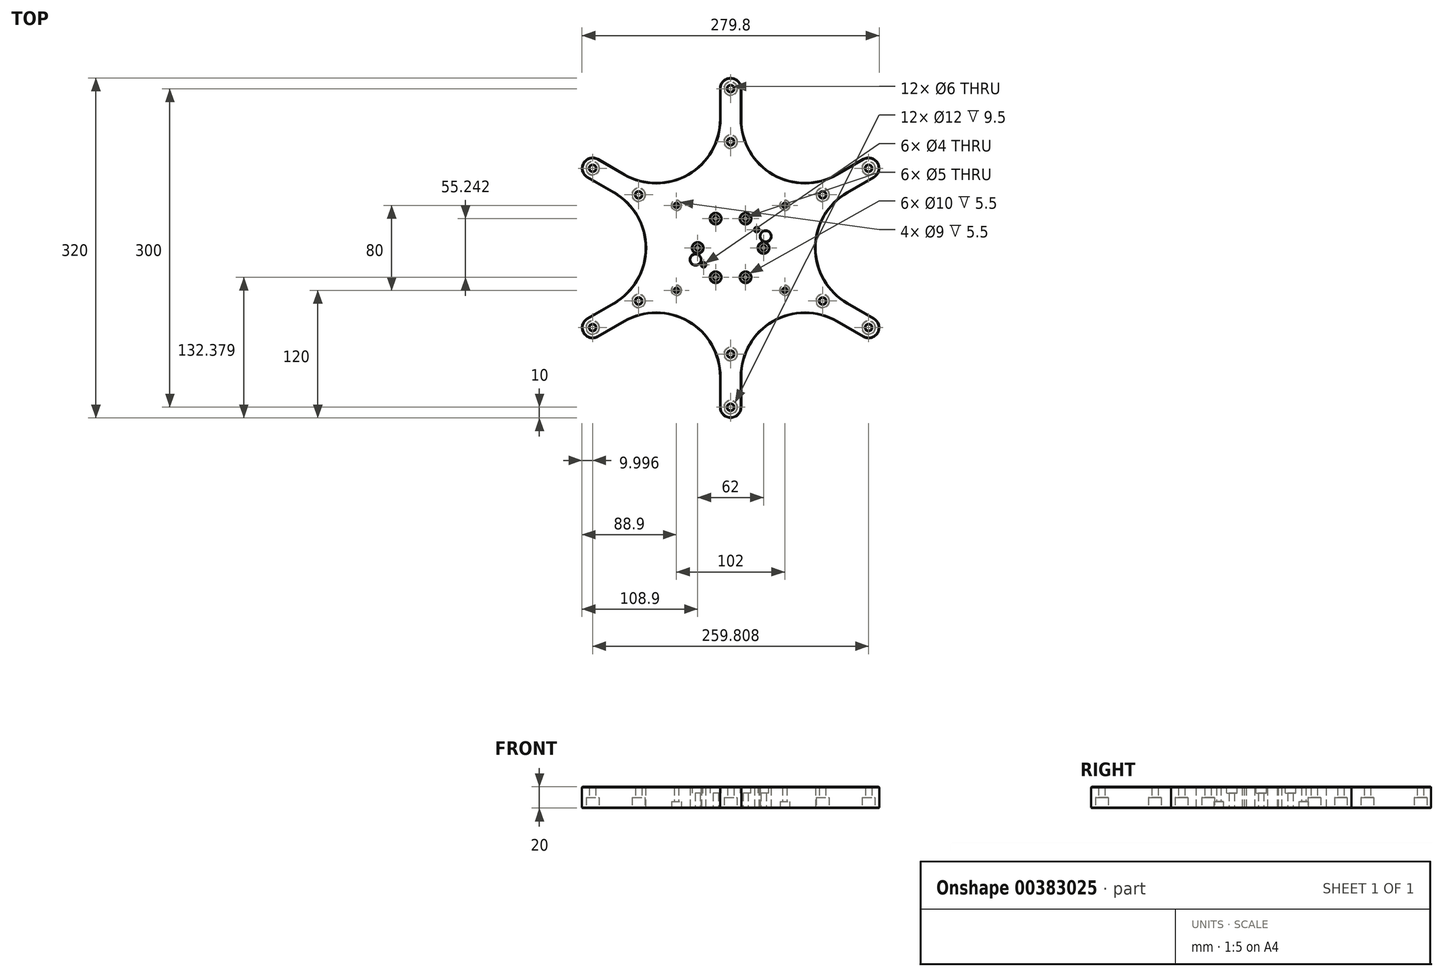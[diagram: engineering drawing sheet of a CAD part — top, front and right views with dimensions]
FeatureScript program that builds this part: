
annotation { "Feature Type Name" : "Feature", "Feature Type Description" : "" }
export const myFeature = defineFeature(function(context is Context, id is Id, definition is map)
    precondition{}
    {
        {
            var Q0;
            Q0=qCreatedBy(makeId("Top.planeOp"),FACE);
            var sketch = newSketch(context, id + "F0", { "sketchPlane" : qUnion([Q0])});
            skCircle(sketch, "E0", {"center": v(31, 0) * mm, "radius": 2.5 * mm});
            skCircle(sketch, "E1.1.0", {"center": v(14.07, 27.62) * mm, "radius": 2.5 * mm});
            skCircle(sketch, "E1.2.0", {"center": v(-14.07, 27.62) * mm, "radius": 2.5 * mm});
            skCircle(sketch, "E1.3.0", {"center": v(-31, 0) * mm, "radius": 2.5 * mm});
            skCircle(sketch, "E1.4.0", {"center": v(-14.07, -27.62) * mm, "radius": 2.5 * mm});
            skCircle(sketch, "E1.5.0", {"center": v(14.07, -27.62) * mm, "radius": 2.5 * mm});
            skPoint(sketch, "E1.center", {"position": v(0, 0) * mm});
            skLineSegment(sketch, "E2.bottom", {"start": v(-56, 45) * mm, "end": v(56, 45) * mm});
            skLineSegment(sketch, "E2.top", {"start": v(-56, -45) * mm, "end": v(56, -45) * mm});
            skLineSegment(sketch, "E2.left", {"start": v(-56, 45) * mm, "end": v(-56, -45) * mm});
            skLineSegment(sketch, "E2.right", {"start": v(56, 45) * mm, "end": v(56, -45) * mm});
            skLineSegment(sketch, "E3", {"start": v(-37.37, 11) * mm, "end": v(33, 11) * mm, "construction": true});
            skLineSegment(sketch, "E4", {"start": v(33, 11) * mm, "end": v(33, -11) * mm, "construction": true});
            skLineSegment(sketch, "E5", {"start": v(33, -11) * mm, "end": v(-33, -11) * mm, "construction": true});
            skLineSegment(sketch, "E6", {"start": v(-33, -11) * mm, "end": v(-33, 11) * mm, "construction": true});
            skCircle(sketch, "E7", {"center": v(-33, 11) * mm, "radius": 5 * mm, "construction": true});
            skCircle(sketch, "E8", {"center": v(33, 11) * mm, "radius": 5 * mm});
            skCircle(sketch, "E9", {"center": v(33, -11) * mm, "radius": 5 * mm, "construction": true});
            skCircle(sketch, "E10", {"center": v(-33, -11) * mm, "radius": 5 * mm});
            skLineSegment(sketch, "E11.bottom", {"start": v(-51, 40) * mm, "end": v(51, 40) * mm, "construction": true});
            skLineSegment(sketch, "E11.top", {"start": v(-51, -40) * mm, "end": v(51, -40) * mm, "construction": true});
            skLineSegment(sketch, "E11.left", {"start": v(-51, 40) * mm, "end": v(-51, -40) * mm, "construction": true});
            skLineSegment(sketch, "E11.right", {"start": v(51, 40) * mm, "end": v(51, -40) * mm, "construction": true});
            skCircle(sketch, "E12", {"center": v(-51, 40) * mm, "radius": 2 * mm});
            skCircle(sketch, "E13", {"center": v(51, 40) * mm, "radius": 2 * mm});
            skCircle(sketch, "E14", {"center": v(51, -40) * mm, "radius": 2 * mm});
            skCircle(sketch, "E15", {"center": v(-51, -40) * mm, "radius": 2 * mm});
            skLineSegment(sketch, "E16", {"start": v(-14.07, -27.62) * mm, "end": v(14.07, 27.62) * mm, "construction": true});
            skLineSegment(sketch, "E17", {"start": v(14.07, -27.62) * mm, "end": v(-14.07, 27.62) * mm, "construction": true});
            skLineSegment(sketch, "E18", {"start": v(55.41, 17.21) * mm, "end": v(-51.67, 17.2) * mm, "construction": true});
            skLineSegment(sketch, "E19", {"start": v(24.57, -95.5) * mm, "end": v(24.57, 92.97) * mm, "construction": true});
            skCircle(sketch, "E20", {"center": v(24.57, 17.21) * mm, "radius": 2 * mm});
            skCircle(sketch, "E21", {"center": v(-25.44, -15.9) * mm, "radius": 2 * mm});
            skSolve(sketch);
        }
        {
            var Q0;
            Q0 = qSketchRegion(id + "F0", true);
            extrude(context, id + "F1", {"entities" : qUnion([Q0]), "depth" : 20 * mm, "offsetDistance" : 25 * mm});
        }
        {
            var Q0;
            Q0=makeQuery(id+"F1.opExtrude","SWEPT_EDGE",EDGE,{"disambiguationData":[OSD([sQuery(id+"F0.wireOp",EDGE,"E2.top"),sQuery(id+"F0.wireOp",EDGE,"E2.left")])]});
            var Q1;
            Q1=makeQuery(id+"F1.opExtrude","SWEPT_EDGE",EDGE,{"disambiguationData":[OSD([sQuery(id+"F0.wireOp",EDGE,"E2.bottom"),sQuery(id+"F0.wireOp",EDGE,"E2.left")])]});
            var Q2;
            Q2=makeQuery(id+"F1.opExtrude","SWEPT_EDGE",EDGE,{"disambiguationData":[OSD([sQuery(id+"F0.wireOp",EDGE,"E2.top"),sQuery(id+"F0.wireOp",EDGE,"E2.right")])]});
            var Q3;
            Q3=makeQuery(id+"F1.opExtrude","SWEPT_EDGE",EDGE,{"disambiguationData":[OSD([sQuery(id+"F0.wireOp",EDGE,"E2.bottom"),sQuery(id+"F0.wireOp",EDGE,"E2.right")])]});
            chamfer(context, id + "F2", {"entities" : qUnion([Q0, Q1, Q2, Q3]), "width" : 2.5 * mm, "tangentPropagation" : true});
        }
        {
            var Q0;
            Q0=makeQuery(id+"F1.opExtrude","CAP_FACE",FACE,{"disambiguationData":[OSD([sQuery(id+"F0.wireOp",EDGE,"E0"),sQuery(id+"F0.wireOp",EDGE,"E1.1.0"),sQuery(id+"F0.wireOp",EDGE,"E1.2.0"),sQuery(id+"F0.wireOp",EDGE,"E1.3.0"),sQuery(id+"F0.wireOp",EDGE,"E1.4.0"),sQuery(id+"F0.wireOp",EDGE,"E1.5.0"),sQuery(id+"F0.wireOp",EDGE,"E2.bottom"),sQuery(id+"F0.wireOp",EDGE,"E2.top"),sQuery(id+"F0.wireOp",EDGE,"E2.left"),sQuery(id+"F0.wireOp",EDGE,"E2.right"),sQuery(id+"F0.wireOp",EDGE,"E7"),sQuery(id+"F0.wireOp",EDGE,"E8"),sQuery(id+"F0.wireOp",EDGE,"E9"),sQuery(id+"F0.wireOp",EDGE,"E10"),sQuery(id+"F0.wireOp",EDGE,"E12"),sQuery(id+"F0.wireOp",EDGE,"E13"),sQuery(id+"F0.wireOp",EDGE,"E14"),sQuery(id+"F0.wireOp",EDGE,"E15")])],"isStart":false});
            var sketch = newSketch(context, id + "F3", { "sketchPlane" : qUnion([Q0])});
            skCircle(sketch, "E22", {"center": v(-14.07, 27.62) * mm, "radius": 5 * mm});
            skCircle(sketch, "E23", {"center": v(14.07, 27.62) * mm, "radius": 5 * mm});
            skCircle(sketch, "E24", {"center": v(31, 0) * mm, "radius": 5 * mm});
            skCircle(sketch, "E25", {"center": v(14.07, -27.62) * mm, "radius": 5 * mm});
            skCircle(sketch, "E26", {"center": v(-14.07, -27.62) * mm, "radius": 5 * mm});
            skCircle(sketch, "E27", {"center": v(-31, 0) * mm, "radius": 5 * mm});
            skSolve(sketch);
        }
        {
            var Q0;
            Q0 = qSketchRegion(id + "F3", true);
            extrude(context, id + "F4", {"entities" : qUnion([Q0]), "operationType" : NewBodyOperationType.REMOVE, "oppositeDirection" : true, "depth" : 6 * mm, "offsetDistance" : 25 * mm});
        }
        {
            var Q0;
            Q0=makeQuery(id+"F1.opExtrude","CAP_FACE",FACE,{"disambiguationData":[OSD([sQuery(id+"F0.wireOp",EDGE,"E0"),sQuery(id+"F0.wireOp",EDGE,"E1.1.0"),sQuery(id+"F0.wireOp",EDGE,"E1.2.0"),sQuery(id+"F0.wireOp",EDGE,"E1.3.0"),sQuery(id+"F0.wireOp",EDGE,"E1.4.0"),sQuery(id+"F0.wireOp",EDGE,"E1.5.0"),sQuery(id+"F0.wireOp",EDGE,"E2.bottom"),sQuery(id+"F0.wireOp",EDGE,"E2.top"),sQuery(id+"F0.wireOp",EDGE,"E2.left"),sQuery(id+"F0.wireOp",EDGE,"E2.right"),sQuery(id+"F0.wireOp",EDGE,"E8"),sQuery(id+"F0.wireOp",EDGE,"E10"),sQuery(id+"F0.wireOp",EDGE,"E12"),sQuery(id+"F0.wireOp",EDGE,"E13"),sQuery(id+"F0.wireOp",EDGE,"E14"),sQuery(id+"F0.wireOp",EDGE,"E15")])],"isStart":true});
            var sketch = newSketch(context, id + "F5", { "sketchPlane" : qUnion([Q0])});
            skCircle(sketch, "E28", {"center": v(-51, 40) * mm, "radius": 4.5 * mm});
            skCircle(sketch, "E29", {"center": v(51, 40) * mm, "radius": 4.5 * mm});
            skCircle(sketch, "E30", {"center": v(51, -40) * mm, "radius": 4.5 * mm});
            skCircle(sketch, "E31", {"center": v(-51, -40) * mm, "radius": 4.5 * mm});
            skSolve(sketch);
        }
        {
            var Q0;
            Q0 = qSketchRegion(id + "F5", true);
            extrude(context, id + "F6", {"entities" : qUnion([Q0]), "operationType" : NewBodyOperationType.REMOVE, "oppositeDirection" : true, "depth" : 6 * mm, "offsetDistance" : 25 * mm});
        }
        {
            var Q0;
            Q0=makeQuery(id+"F1.opExtrude","CAP_FACE",FACE,{"disambiguationData":[OSD([sQuery(id+"F0.wireOp",EDGE,"E0"),sQuery(id+"F0.wireOp",EDGE,"E1.1.0"),sQuery(id+"F0.wireOp",EDGE,"E1.2.0"),sQuery(id+"F0.wireOp",EDGE,"E1.3.0"),sQuery(id+"F0.wireOp",EDGE,"E1.4.0"),sQuery(id+"F0.wireOp",EDGE,"E1.5.0"),sQuery(id+"F0.wireOp",EDGE,"E2.bottom"),sQuery(id+"F0.wireOp",EDGE,"E2.top"),sQuery(id+"F0.wireOp",EDGE,"E2.left"),sQuery(id+"F0.wireOp",EDGE,"E2.right"),sQuery(id+"F0.wireOp",EDGE,"E8"),sQuery(id+"F0.wireOp",EDGE,"E10"),sQuery(id+"F0.wireOp",EDGE,"E12"),sQuery(id+"F0.wireOp",EDGE,"E13"),sQuery(id+"F0.wireOp",EDGE,"E14"),sQuery(id+"F0.wireOp",EDGE,"E15")])],"isStart":true});
            var sketch = newSketch(context, id + "F7", { "sketchPlane" : qUnion([Q0])});
            skLineSegment(sketch, "E32", {"start": v(0, 0) * mm, "end": v(0, 187.02) * mm, "construction": true});
            skCircle(sketch, "E33", {"center": v(0, 150) * mm, "radius": 3 * mm});
            skCircle(sketch, "E34", {"center": v(0, 100) * mm, "radius": 3 * mm});
            skCircle(sketch, "E35", {"center": v(0, 150) * mm, "radius": 10 * mm, "construction": true});
            skLineSegment(sketch, "E36", {"start": v(-10, 150) * mm, "end": v(-10, 35.87) * mm, "construction": true});
            skLineSegment(sketch, "E37", {"start": v(10, 39.07) * mm, "end": v(10, 150) * mm, "construction": true});
            skLineSegment(sketch, "E38.1.0", {"start": v(0, 0) * mm, "end": v(-161.97, 93.51) * mm, "construction": true});
            skCircle(sketch, "E38.1.1", {"center": v(-129.9, 75) * mm, "radius": 10 * mm, "construction": true});
            skCircle(sketch, "E38.1.2", {"center": v(-129.9, 75) * mm, "radius": 3 * mm});
            skLineSegment(sketch, "E38.1.3", {"start": v(-134.9, 66.34) * mm, "end": v(-36.06, 9.27) * mm, "construction": true});
            skLineSegment(sketch, "E38.1.4", {"start": v(-28.84, 28.2) * mm, "end": v(-124.9, 83.66) * mm, "construction": true});
            skCircle(sketch, "E38.1.5", {"center": v(-86.6, 50) * mm, "radius": 3 * mm});
            skLineSegment(sketch, "E38.2.0", {"start": v(0, 0) * mm, "end": v(-161.97, -93.51) * mm, "construction": true});
            skCircle(sketch, "E38.2.1", {"center": v(-129.9, -75) * mm, "radius": 10 * mm, "construction": true});
            skCircle(sketch, "E38.2.2", {"center": v(-129.9, -75) * mm, "radius": 3 * mm});
            skLineSegment(sketch, "E38.2.3", {"start": v(-124.9, -83.66) * mm, "end": v(-26.06, -26.6) * mm, "construction": true});
            skLineSegment(sketch, "E38.2.4", {"start": v(-38.84, -10.88) * mm, "end": v(-134.9, -66.34) * mm, "construction": true});
            skCircle(sketch, "E38.2.5", {"center": v(-86.6, -50) * mm, "radius": 3 * mm});
            skLineSegment(sketch, "E38.3.0", {"start": v(0, 0) * mm, "end": v(0, -187.02) * mm, "construction": true});
            skCircle(sketch, "E38.3.1", {"center": v(0, -150) * mm, "radius": 10 * mm, "construction": true});
            skCircle(sketch, "E38.3.2", {"center": v(0, -150) * mm, "radius": 3 * mm});
            skLineSegment(sketch, "E38.3.3", {"start": v(10, -150) * mm, "end": v(10, -35.87) * mm, "construction": true});
            skLineSegment(sketch, "E38.3.4", {"start": v(-10, -39.07) * mm, "end": v(-10, -150) * mm, "construction": true});
            skCircle(sketch, "E38.3.5", {"center": v(0, -100) * mm, "radius": 3 * mm});
            skLineSegment(sketch, "E38.4.0", {"start": v(0, 0) * mm, "end": v(161.97, -93.51) * mm, "construction": true});
            skCircle(sketch, "E38.4.1", {"center": v(129.9, -75) * mm, "radius": 10 * mm, "construction": true});
            skCircle(sketch, "E38.4.2", {"center": v(129.9, -75) * mm, "radius": 3 * mm});
            skLineSegment(sketch, "E38.4.3", {"start": v(134.9, -66.34) * mm, "end": v(36.06, -9.27) * mm, "construction": true});
            skLineSegment(sketch, "E38.4.4", {"start": v(28.84, -28.2) * mm, "end": v(124.9, -83.66) * mm, "construction": true});
            skCircle(sketch, "E38.4.5", {"center": v(86.6, -50) * mm, "radius": 3 * mm});
            skLineSegment(sketch, "E38.5.0", {"start": v(0, 0) * mm, "end": v(161.97, 93.51) * mm, "construction": true});
            skCircle(sketch, "E38.5.1", {"center": v(129.9, 75) * mm, "radius": 10 * mm, "construction": true});
            skCircle(sketch, "E38.5.2", {"center": v(129.9, 75) * mm, "radius": 3 * mm});
            skLineSegment(sketch, "E38.5.3", {"start": v(124.9, 83.66) * mm, "end": v(26.06, 26.6) * mm, "construction": true});
            skLineSegment(sketch, "E38.5.4", {"start": v(38.84, 10.88) * mm, "end": v(134.9, 66.34) * mm, "construction": true});
            skCircle(sketch, "E38.5.5", {"center": v(86.6, 50) * mm, "radius": 3 * mm});
            skPoint(sketch, "E38.center", {"position": v(0, 0) * mm});
            skArc(sketch, "E39", {"start": v(-100, 69.28) * mm, "mid": v(-40, 69.28) * mm, "end": v(-10, 121.24) * mm});
            skArc(sketch, "E40", {"start": v(10, 121.24) * mm, "mid": v(40, 69.28) * mm, "end": v(100, 69.28) * mm});
            skArc(sketch, "E41", {"start": v(110, 51.96) * mm, "mid": v(80, 0) * mm, "end": v(110, -51.96) * mm});
            skArc(sketch, "E42", {"start": v(100, -69.28) * mm, "mid": v(40, -69.28) * mm, "end": v(10, -121.24) * mm});
            skArc(sketch, "E43", {"start": v(-10, -121.24) * mm, "mid": v(-40, -69.28) * mm, "end": v(-100, -69.28) * mm});
            skArc(sketch, "E44", {"start": v(-110, -51.96) * mm, "mid": v(-80, 0) * mm, "end": v(-110, 51.96) * mm});
            skLineSegment(sketch, "E45", {"start": v(-100, 69.28) * mm, "end": v(-124.9, 83.66) * mm});
            skLineSegment(sketch, "E46", {"start": v(-110, 51.96) * mm, "end": v(-134.9, 66.34) * mm});
            skLineSegment(sketch, "E47", {"start": v(-110, -51.96) * mm, "end": v(-134.9, -66.34) * mm});
            skLineSegment(sketch, "E48", {"start": v(-100, -69.28) * mm, "end": v(-124.9, -83.66) * mm});
            skLineSegment(sketch, "E49", {"start": v(-10, -121.24) * mm, "end": v(-10, -150) * mm});
            skLineSegment(sketch, "E50", {"start": v(10, -121.24) * mm, "end": v(10, -150) * mm});
            skLineSegment(sketch, "E51", {"start": v(100, -69.28) * mm, "end": v(124.9, -83.66) * mm});
            skLineSegment(sketch, "E52", {"start": v(134.9, -66.34) * mm, "end": v(110, -51.96) * mm});
            skLineSegment(sketch, "E53", {"start": v(110, 51.96) * mm, "end": v(134.9, 66.34) * mm});
            skLineSegment(sketch, "E54", {"start": v(124.9, 83.66) * mm, "end": v(100, 69.28) * mm});
            skLineSegment(sketch, "E55", {"start": v(10, 121.24) * mm, "end": v(10, 150) * mm});
            skLineSegment(sketch, "E56", {"start": v(-10, 121.24) * mm, "end": v(-10, 150) * mm});
            skArc(sketch, "E57", {"start": v(-124.9, 83.66) * mm, "mid": v(-138.56, 80) * mm, "end": v(-134.9, 66.34) * mm});
            skArc(sketch, "E58", {"start": v(-134.9, -66.34) * mm, "mid": v(-138.56, -80) * mm, "end": v(-124.9, -83.66) * mm});
            skArc(sketch, "E59", {"start": v(-10, -150) * mm, "mid": v(0, -160) * mm, "end": v(10, -150) * mm});
            skArc(sketch, "E60", {"start": v(124.9, -83.66) * mm, "mid": v(138.56, -80) * mm, "end": v(134.9, -66.34) * mm});
            skArc(sketch, "E61", {"start": v(134.9, 66.34) * mm, "mid": v(138.56, 80) * mm, "end": v(124.9, 83.66) * mm});
            skArc(sketch, "E62", {"start": v(10, 150) * mm, "mid": v(0, 160) * mm, "end": v(-10, 150) * mm});
            skLineSegment(sketch, "E63.0.0", {"start": v(-53.5, -45) * mm, "end": v(53.5, -45) * mm});
            skLineSegment(sketch, "E63.0.1", {"start": v(53.5, -45) * mm, "end": v(56, -42.5) * mm});
            skLineSegment(sketch, "E63.0.2", {"start": v(56, -42.5) * mm, "end": v(56, 42.5) * mm});
            skLineSegment(sketch, "E63.0.3", {"start": v(56, 42.5) * mm, "end": v(53.5, 45) * mm});
            skLineSegment(sketch, "E63.0.4", {"start": v(53.5, 45) * mm, "end": v(-53.5, 45) * mm});
            skLineSegment(sketch, "E63.0.5", {"start": v(-53.5, 45) * mm, "end": v(-56, 42.5) * mm});
            skLineSegment(sketch, "E63.0.6", {"start": v(-56, 42.5) * mm, "end": v(-56, -42.5) * mm});
            skLineSegment(sketch, "E63.0.7", {"start": v(-56, -42.5) * mm, "end": v(-53.5, -45) * mm});
            skSolve(sketch);
        }
        {
            var Q0;
            Q0 = qSketchRegion(id + "F7", true);
            var Q1;
            Q1=makeQuery(id+"F1.opExtrude","CAP_FACE",FACE,{"disambiguationData":[OSD([sQuery(id+"F0.wireOp",EDGE,"E0"),sQuery(id+"F0.wireOp",EDGE,"E1.1.0"),sQuery(id+"F0.wireOp",EDGE,"E1.2.0"),sQuery(id+"F0.wireOp",EDGE,"E1.3.0"),sQuery(id+"F0.wireOp",EDGE,"E1.4.0"),sQuery(id+"F0.wireOp",EDGE,"E1.5.0"),sQuery(id+"F0.wireOp",EDGE,"E2.bottom"),sQuery(id+"F0.wireOp",EDGE,"E2.top"),sQuery(id+"F0.wireOp",EDGE,"E2.left"),sQuery(id+"F0.wireOp",EDGE,"E2.right"),sQuery(id+"F0.wireOp",EDGE,"E8"),sQuery(id+"F0.wireOp",EDGE,"E10"),sQuery(id+"F0.wireOp",EDGE,"E12"),sQuery(id+"F0.wireOp",EDGE,"E13"),sQuery(id+"F0.wireOp",EDGE,"E14"),sQuery(id+"F0.wireOp",EDGE,"E15")])],"isStart":false});
            extrude(context, id + "F8", {"entities" : qUnion([Q0]), "operationType" : NewBodyOperationType.ADD, "endBound" : BoundingType.UP_TO_SURFACE, "oppositeDirection" : true, "depth" : 25 * mm, "endBoundEntityFace" : qUnion([Q1]), "offsetDistance" : 25 * mm});
        }
        {
            var Q0;
            Q0=makeQuery(id+"F8.boolean.opBoolean","MERGE",FACE,{"derivedFrom":[makeQuery(id+"F1.opExtrude","CAP_FACE",FACE,{"disambiguationData":[OSD([sQuery(id+"F0.wireOp",EDGE,"E0"),sQuery(id+"F0.wireOp",EDGE,"E1.1.0"),sQuery(id+"F0.wireOp",EDGE,"E1.2.0"),sQuery(id+"F0.wireOp",EDGE,"E1.3.0"),sQuery(id+"F0.wireOp",EDGE,"E1.4.0"),sQuery(id+"F0.wireOp",EDGE,"E1.5.0"),sQuery(id+"F0.wireOp",EDGE,"E2.bottom"),sQuery(id+"F0.wireOp",EDGE,"E2.top"),sQuery(id+"F0.wireOp",EDGE,"E2.left"),sQuery(id+"F0.wireOp",EDGE,"E2.right"),sQuery(id+"F0.wireOp",EDGE,"E8"),sQuery(id+"F0.wireOp",EDGE,"E10"),sQuery(id+"F0.wireOp",EDGE,"E12"),sQuery(id+"F0.wireOp",EDGE,"E13"),sQuery(id+"F0.wireOp",EDGE,"E14"),sQuery(id+"F0.wireOp",EDGE,"E15")])],"isStart":true}),makeQuery(id+"F8.opExtrude","CAP_FACE",FACE,{"disambiguationData":[OSD([sQuery(id+"F7.wireOp",EDGE,"E33"),sQuery(id+"F7.wireOp",EDGE,"E34"),sQuery(id+"F7.wireOp",EDGE,"E38.1.2"),sQuery(id+"F7.wireOp",EDGE,"E38.1.5"),sQuery(id+"F7.wireOp",EDGE,"E38.2.2"),sQuery(id+"F7.wireOp",EDGE,"E38.2.5"),sQuery(id+"F7.wireOp",EDGE,"E38.3.2"),sQuery(id+"F7.wireOp",EDGE,"E38.3.5"),sQuery(id+"F7.wireOp",EDGE,"E38.4.2"),sQuery(id+"F7.wireOp",EDGE,"E38.4.5"),sQuery(id+"F7.wireOp",EDGE,"E38.5.2"),sQuery(id+"F7.wireOp",EDGE,"E38.5.5"),sQuery(id+"F7.wireOp",EDGE,"E39"),sQuery(id+"F7.wireOp",EDGE,"E40"),sQuery(id+"F7.wireOp",EDGE,"E41"),sQuery(id+"F7.wireOp",EDGE,"E42"),sQuery(id+"F7.wireOp",EDGE,"E43"),sQuery(id+"F7.wireOp",EDGE,"E44"),sQuery(id+"F7.wireOp",EDGE,"E45"),sQuery(id+"F7.wireOp",EDGE,"E46"),sQuery(id+"F7.wireOp",EDGE,"E47"),sQuery(id+"F7.wireOp",EDGE,"E48"),sQuery(id+"F7.wireOp",EDGE,"E49"),sQuery(id+"F7.wireOp",EDGE,"E50"),sQuery(id+"F7.wireOp",EDGE,"E51"),sQuery(id+"F7.wireOp",EDGE,"E52"),sQuery(id+"F7.wireOp",EDGE,"E53"),sQuery(id+"F7.wireOp",EDGE,"E54"),sQuery(id+"F7.wireOp",EDGE,"E55"),sQuery(id+"F7.wireOp",EDGE,"E56"),sQuery(id+"F7.wireOp",EDGE,"E57"),sQuery(id+"F7.wireOp",EDGE,"E58"),sQuery(id+"F7.wireOp",EDGE,"E59"),sQuery(id+"F7.wireOp",EDGE,"E60"),sQuery(id+"F7.wireOp",EDGE,"E61"),sQuery(id+"F7.wireOp",EDGE,"E62"),sQuery(id+"F7.wireOp",EDGE,"E63.0.0"),sQuery(id+"F7.wireOp",EDGE,"E63.0.1"),sQuery(id+"F7.wireOp",EDGE,"E63.0.2"),sQuery(id+"F7.wireOp",EDGE,"E63.0.3"),sQuery(id+"F7.wireOp",EDGE,"E63.0.4"),sQuery(id+"F7.wireOp",EDGE,"E63.0.5"),sQuery(id+"F7.wireOp",EDGE,"E63.0.6"),sQuery(id+"F7.wireOp",EDGE,"E63.0.7")])],"isStart":true})]});
            var sketch = newSketch(context, id + "F9", { "sketchPlane" : qUnion([Q0])});
            skCircle(sketch, "E64", {"center": v(0, 150) * mm, "radius": 6 * mm});
            skCircle(sketch, "E65", {"center": v(0, 100) * mm, "radius": 6 * mm});
            skCircle(sketch, "E66", {"center": v(129.9, 75) * mm, "radius": 6 * mm});
            skCircle(sketch, "E67", {"center": v(86.6, 50) * mm, "radius": 6 * mm});
            skCircle(sketch, "E68", {"center": v(86.6, -50) * mm, "radius": 6 * mm});
            skCircle(sketch, "E69", {"center": v(129.9, -75) * mm, "radius": 6 * mm});
            skCircle(sketch, "E70", {"center": v(0, -100) * mm, "radius": 6 * mm});
            skCircle(sketch, "E71", {"center": v(0, -150) * mm, "radius": 6 * mm});
            skCircle(sketch, "E72", {"center": v(-86.6, -50) * mm, "radius": 6 * mm});
            skCircle(sketch, "E73", {"center": v(-129.9, -75) * mm, "radius": 6 * mm});
            skCircle(sketch, "E74", {"center": v(-86.6, 50) * mm, "radius": 6 * mm});
            skCircle(sketch, "E75", {"center": v(-129.9, 75) * mm, "radius": 6 * mm});
            skSolve(sketch);
        }
        {
            var Q0;
            Q0 = qSketchRegion(id + "F9", true);
            extrude(context, id + "F10", {"entities" : qUnion([Q0]), "operationType" : NewBodyOperationType.REMOVE, "oppositeDirection" : true, "depth" : 10 * mm, "offsetDistance" : 25 * mm});
        }
        {
            var Q0;
            Q0=makeQuery(id+"F8.boolean.opBoolean","MERGE",FACE,{"derivedFrom":[makeQuery(id+"F1.opExtrude","CAP_FACE",FACE,{"disambiguationData":[OSD([sQuery(id+"F0.wireOp",EDGE,"E0"),sQuery(id+"F0.wireOp",EDGE,"E1.1.0"),sQuery(id+"F0.wireOp",EDGE,"E1.2.0"),sQuery(id+"F0.wireOp",EDGE,"E1.3.0"),sQuery(id+"F0.wireOp",EDGE,"E1.4.0"),sQuery(id+"F0.wireOp",EDGE,"E1.5.0"),sQuery(id+"F0.wireOp",EDGE,"E2.bottom"),sQuery(id+"F0.wireOp",EDGE,"E2.top"),sQuery(id+"F0.wireOp",EDGE,"E2.left"),sQuery(id+"F0.wireOp",EDGE,"E2.right"),sQuery(id+"F0.wireOp",EDGE,"E8"),sQuery(id+"F0.wireOp",EDGE,"E10"),sQuery(id+"F0.wireOp",EDGE,"E12"),sQuery(id+"F0.wireOp",EDGE,"E13"),sQuery(id+"F0.wireOp",EDGE,"E14"),sQuery(id+"F0.wireOp",EDGE,"E15")])],"isStart":false}),makeQuery(id+"F8.opExtrude","CAP_FACE",FACE,{"disambiguationData":[OSD([sQuery(id+"F7.wireOp",EDGE,"E33"),sQuery(id+"F7.wireOp",EDGE,"E34"),sQuery(id+"F7.wireOp",EDGE,"E38.1.2"),sQuery(id+"F7.wireOp",EDGE,"E38.1.5"),sQuery(id+"F7.wireOp",EDGE,"E38.2.2"),sQuery(id+"F7.wireOp",EDGE,"E38.2.5"),sQuery(id+"F7.wireOp",EDGE,"E38.3.2"),sQuery(id+"F7.wireOp",EDGE,"E38.3.5"),sQuery(id+"F7.wireOp",EDGE,"E38.4.2"),sQuery(id+"F7.wireOp",EDGE,"E38.4.5"),sQuery(id+"F7.wireOp",EDGE,"E38.5.2"),sQuery(id+"F7.wireOp",EDGE,"E38.5.5"),sQuery(id+"F7.wireOp",EDGE,"E39"),sQuery(id+"F7.wireOp",EDGE,"E40"),sQuery(id+"F7.wireOp",EDGE,"E41"),sQuery(id+"F7.wireOp",EDGE,"E42"),sQuery(id+"F7.wireOp",EDGE,"E43"),sQuery(id+"F7.wireOp",EDGE,"E44"),sQuery(id+"F7.wireOp",EDGE,"E45"),sQuery(id+"F7.wireOp",EDGE,"E46"),sQuery(id+"F7.wireOp",EDGE,"E47"),sQuery(id+"F7.wireOp",EDGE,"E48"),sQuery(id+"F7.wireOp",EDGE,"E49"),sQuery(id+"F7.wireOp",EDGE,"E50"),sQuery(id+"F7.wireOp",EDGE,"E51"),sQuery(id+"F7.wireOp",EDGE,"E52"),sQuery(id+"F7.wireOp",EDGE,"E53"),sQuery(id+"F7.wireOp",EDGE,"E54"),sQuery(id+"F7.wireOp",EDGE,"E55"),sQuery(id+"F7.wireOp",EDGE,"E56"),sQuery(id+"F7.wireOp",EDGE,"E57"),sQuery(id+"F7.wireOp",EDGE,"E58"),sQuery(id+"F7.wireOp",EDGE,"E59"),sQuery(id+"F7.wireOp",EDGE,"E60"),sQuery(id+"F7.wireOp",EDGE,"E61"),sQuery(id+"F7.wireOp",EDGE,"E62"),sQuery(id+"F7.wireOp",EDGE,"E63.0.0"),sQuery(id+"F7.wireOp",EDGE,"E63.0.1"),sQuery(id+"F7.wireOp",EDGE,"E63.0.2"),sQuery(id+"F7.wireOp",EDGE,"E63.0.3"),sQuery(id+"F7.wireOp",EDGE,"E63.0.4"),sQuery(id+"F7.wireOp",EDGE,"E63.0.5"),sQuery(id+"F7.wireOp",EDGE,"E63.0.6"),sQuery(id+"F7.wireOp",EDGE,"E63.0.7")])],"isStart":false})]});
            var Q1;
            Q1=makeQuery(id+"F8.boolean.opBoolean","MERGE",FACE,{"derivedFrom":[makeQuery(id+"F1.opExtrude","CAP_FACE",FACE,{"disambiguationData":[OSD([sQuery(id+"F0.wireOp",EDGE,"E0"),sQuery(id+"F0.wireOp",EDGE,"E1.1.0"),sQuery(id+"F0.wireOp",EDGE,"E1.2.0"),sQuery(id+"F0.wireOp",EDGE,"E1.3.0"),sQuery(id+"F0.wireOp",EDGE,"E1.4.0"),sQuery(id+"F0.wireOp",EDGE,"E1.5.0"),sQuery(id+"F0.wireOp",EDGE,"E2.bottom"),sQuery(id+"F0.wireOp",EDGE,"E2.top"),sQuery(id+"F0.wireOp",EDGE,"E2.left"),sQuery(id+"F0.wireOp",EDGE,"E2.right"),sQuery(id+"F0.wireOp",EDGE,"E8"),sQuery(id+"F0.wireOp",EDGE,"E10"),sQuery(id+"F0.wireOp",EDGE,"E12"),sQuery(id+"F0.wireOp",EDGE,"E13"),sQuery(id+"F0.wireOp",EDGE,"E14"),sQuery(id+"F0.wireOp",EDGE,"E15")])],"isStart":true}),makeQuery(id+"F8.opExtrude","CAP_FACE",FACE,{"disambiguationData":[OSD([sQuery(id+"F7.wireOp",EDGE,"E33"),sQuery(id+"F7.wireOp",EDGE,"E34"),sQuery(id+"F7.wireOp",EDGE,"E38.1.2"),sQuery(id+"F7.wireOp",EDGE,"E38.1.5"),sQuery(id+"F7.wireOp",EDGE,"E38.2.2"),sQuery(id+"F7.wireOp",EDGE,"E38.2.5"),sQuery(id+"F7.wireOp",EDGE,"E38.3.2"),sQuery(id+"F7.wireOp",EDGE,"E38.3.5"),sQuery(id+"F7.wireOp",EDGE,"E38.4.2"),sQuery(id+"F7.wireOp",EDGE,"E38.4.5"),sQuery(id+"F7.wireOp",EDGE,"E38.5.2"),sQuery(id+"F7.wireOp",EDGE,"E38.5.5"),sQuery(id+"F7.wireOp",EDGE,"E39"),sQuery(id+"F7.wireOp",EDGE,"E40"),sQuery(id+"F7.wireOp",EDGE,"E41"),sQuery(id+"F7.wireOp",EDGE,"E42"),sQuery(id+"F7.wireOp",EDGE,"E43"),sQuery(id+"F7.wireOp",EDGE,"E44"),sQuery(id+"F7.wireOp",EDGE,"E45"),sQuery(id+"F7.wireOp",EDGE,"E46"),sQuery(id+"F7.wireOp",EDGE,"E47"),sQuery(id+"F7.wireOp",EDGE,"E48"),sQuery(id+"F7.wireOp",EDGE,"E49"),sQuery(id+"F7.wireOp",EDGE,"E50"),sQuery(id+"F7.wireOp",EDGE,"E51"),sQuery(id+"F7.wireOp",EDGE,"E52"),sQuery(id+"F7.wireOp",EDGE,"E53"),sQuery(id+"F7.wireOp",EDGE,"E54"),sQuery(id+"F7.wireOp",EDGE,"E55"),sQuery(id+"F7.wireOp",EDGE,"E56"),sQuery(id+"F7.wireOp",EDGE,"E57"),sQuery(id+"F7.wireOp",EDGE,"E58"),sQuery(id+"F7.wireOp",EDGE,"E59"),sQuery(id+"F7.wireOp",EDGE,"E60"),sQuery(id+"F7.wireOp",EDGE,"E61"),sQuery(id+"F7.wireOp",EDGE,"E62"),sQuery(id+"F7.wireOp",EDGE,"E63.0.0"),sQuery(id+"F7.wireOp",EDGE,"E63.0.1"),sQuery(id+"F7.wireOp",EDGE,"E63.0.2"),sQuery(id+"F7.wireOp",EDGE,"E63.0.3"),sQuery(id+"F7.wireOp",EDGE,"E63.0.4"),sQuery(id+"F7.wireOp",EDGE,"E63.0.5"),sQuery(id+"F7.wireOp",EDGE,"E63.0.6"),sQuery(id+"F7.wireOp",EDGE,"E63.0.7")])],"isStart":true})]});
            chamfer(context, id + "F11", {"entities" : qUnion([Q0, Q1]), "width" : 0.5 * mm, "tangentPropagation" : true});
        }
    });
